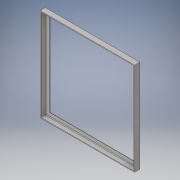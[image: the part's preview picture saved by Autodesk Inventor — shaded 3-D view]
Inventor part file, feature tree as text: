
AUTODESK INVENTOR PART (.ipt)
format: ipt  version: 2016 (Build 200138000, 138)  size: 123,904 bytes
history: native  units: in
note: dims shown in document units (in); Inventor stores cm internally (conversion verified against a paired STEP export)
features: extrude x2, sketch x2, fillet x1
ambient origin geometry x8: Origin, YZ Plane, XZ Plane, XY Plane, X Axis, Y Axis, Z Axis, Center Point
bodies: Solid1 (feature_tree)
feature tree (5):
  extrude  "Extrusion1"  Depth=20.0in
  extrude  "Extrusion2"  Depth=0.1046in TaperAngle=0.0deg
  fillet  "Fillet1"  Radius=1.0in
  sketch  "Sketch1"  dims[d0=20.3125in d1=20.0in]
  sketch  "Sketch2"  dims[d2=1.0in d3=0.1046in d4=0.0in d5=1.0in d6=0.0in d7=0.125in]
